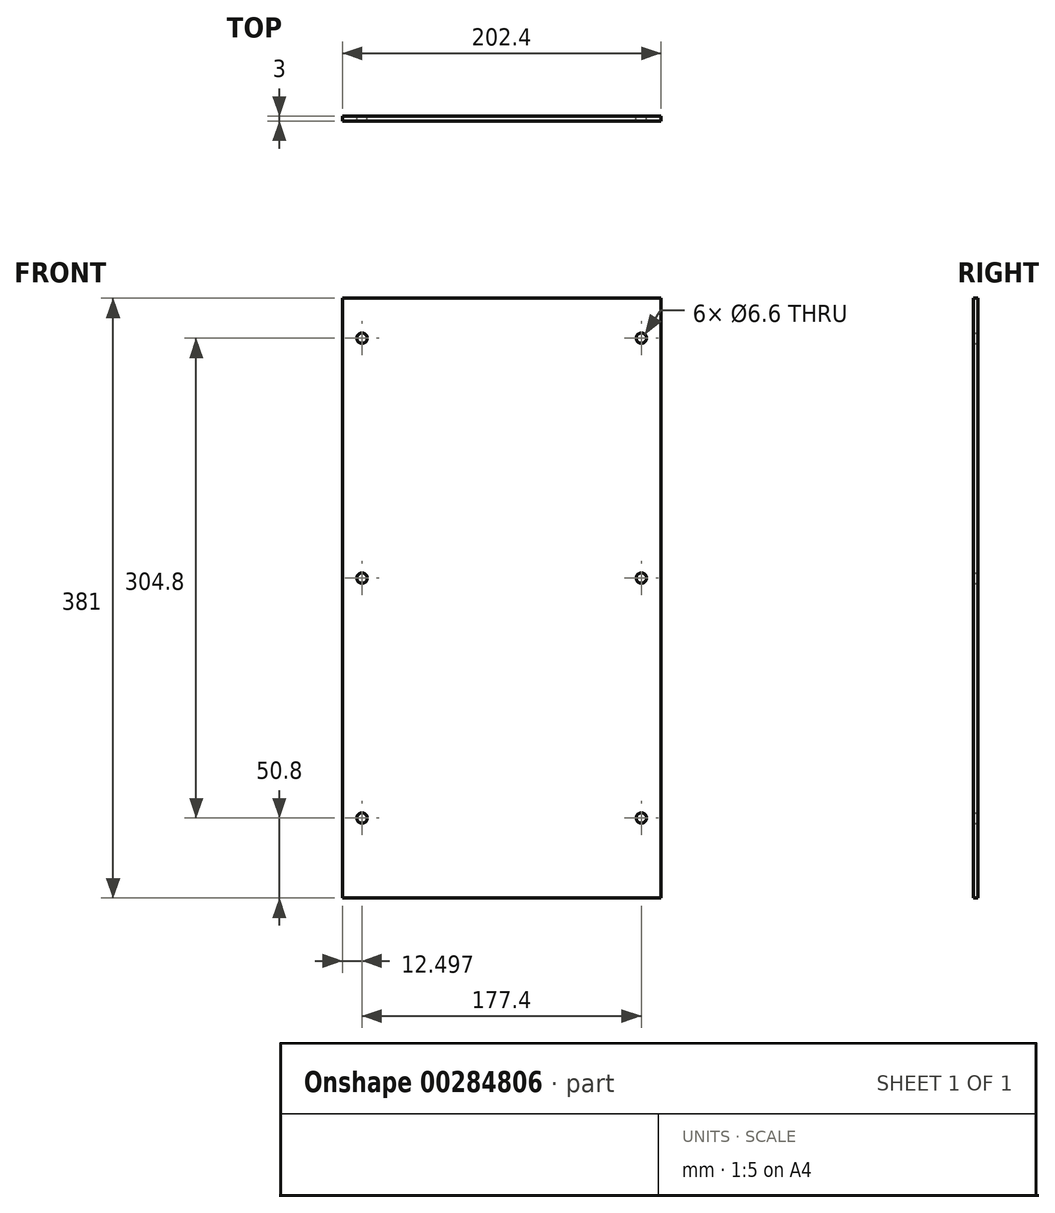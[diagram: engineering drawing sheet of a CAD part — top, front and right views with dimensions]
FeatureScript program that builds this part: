
annotation { "Feature Type Name" : "Feature", "Feature Type Description" : "" }
export const myFeature = defineFeature(function(context is Context, id is Id, definition is map)
    precondition{}
    {
        {
            var Q0;
            Q0=qCreatedBy(makeId("Front.planeOp"),FACE);
            var sketch = newSketch(context, id + "F0", { "sketchPlane" : qUnion([Q0])});
            skLineSegment(sketch, "E0.bottom", {"start": v(-163.16, 188.8) * mm, "end": v(39.24, 188.8) * mm});
            skLineSegment(sketch, "E0.top", {"start": v(-163.16, -192.2) * mm, "end": v(39.24, -192.2) * mm});
            skLineSegment(sketch, "E0.left", {"start": v(-163.16, 188.8) * mm, "end": v(-163.16, -192.2) * mm});
            skLineSegment(sketch, "E0.right", {"start": v(39.24, 188.8) * mm, "end": v(39.24, -192.2) * mm});
            skPoint(sketch, "E1", {"position": v(-150.66, 163.4) * mm});
            skPoint(sketch, "E2", {"position": v(-150.66, 11) * mm});
            skPoint(sketch, "E3", {"position": v(-150.66, -141.4) * mm});
            skPoint(sketch, "E4", {"position": v(26.74, 163.4) * mm});
            skPoint(sketch, "E5", {"position": v(26.74, 11) * mm});
            skPoint(sketch, "E6", {"position": v(26.74, -141.4) * mm});
            skSolve(sketch);
        }
        {
            var Q0;
            Q0 = qSketchRegion(id + "F0", true);
            extrude(context, id + "F1", {"entities" : qUnion([Q0]), "depth" : 3 * mm});
        }
        {
            var Q0;
            Q0=sQuery(id+"F0.wireOp",VERTEX,"E1");
            var Q1;
            Q1=sQuery(id+"F0.wireOp",VERTEX,"E2");
            var Q2;
            Q2=sQuery(id+"F0.wireOp",VERTEX,"E3");
            var Q3;
            Q3=sQuery(id+"F0.wireOp",VERTEX,"E6");
            var Q4;
            Q4=sQuery(id+"F0.wireOp",VERTEX,"E5");
            var Q5;
            Q5=sQuery(id+"F0.wireOp",VERTEX,"E4");
            var Q6;
            Q6=makeQuery(id+"F1.opExtrude","SWEPT_BODY",BODY,{"disambiguationData":[OSD([sQuery(id+"F0.wireOp",EDGE,"E0.bottom"),sQuery(id+"F0.wireOp",EDGE,"E0.top"),sQuery(id+"F0.wireOp",EDGE,"E0.left"),sQuery(id+"F0.wireOp",EDGE,"E0.right")])]});
            hole(context, id + "F2", {"style" : HoleStyle.SIMPLE, "endStyle" : HoleEndStyle.THROUGH, "oppositeDirection" : true, "standardTappedOrClearance" : lookupTablePath({ "standard" : "ISO", "fit" : "Normal", "size" : "M6", "type" : "Clearance" }), "standardBlindInLast" : lookupTablePath({ "fit" : "Standard", "standard" : "ISO", "size" : "M6", "type" : "Clearance" }), "holeDiameter" : 6.6 * mm, "tappedDepth" : 12 * mm, "tapClearance" : 3, "locations" : qUnion([Q0, Q1, Q2, Q3, Q4, Q5]), "scope" : qUnion([Q6])});
        }
    });
